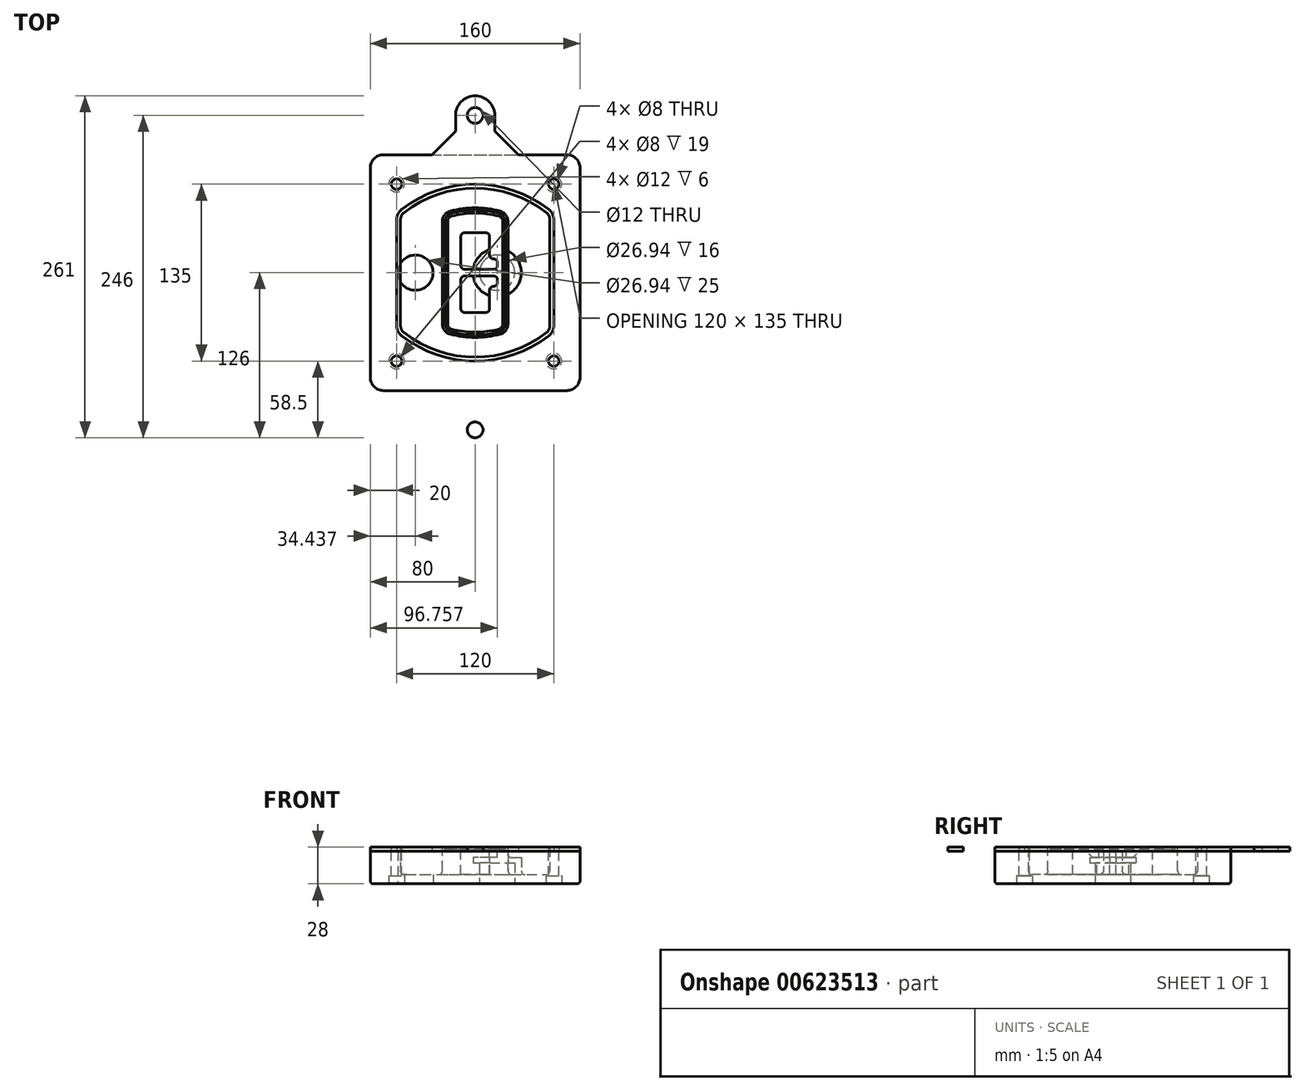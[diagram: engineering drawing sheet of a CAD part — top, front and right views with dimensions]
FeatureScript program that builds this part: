
annotation { "Feature Type Name" : "Feature", "Feature Type Description" : "" }
export const myFeature = defineFeature(function(context is Context, id is Id, definition is map)
    precondition{}
    {
        {
            var Q0;
            Q0=qCreatedBy(makeId("Top.planeOp"),FACE);
            var sketch = newSketch(context, id + "F0", { "sketchPlane" : qUnion([Q0])});
            skPoint(sketch, "E0.rect.middle", {"position": v(0, 0) * mm});
            skLineSegment(sketch, "E1.bottom", {"start": v(-70, -90) * mm, "end": v(70, -90) * mm});
            skLineSegment(sketch, "E1.top", {"start": v(-70, 90) * mm, "end": v(70, 90) * mm});
            skLineSegment(sketch, "E1.left", {"start": v(-80, -80) * mm, "end": v(-80, 80) * mm});
            skLineSegment(sketch, "E1.right", {"start": v(80, -80) * mm, "end": v(80, 80) * mm});
            skLineSegment(sketch, "E2", {"start": v(-80, 90) * mm, "end": v(80, -90) * mm, "construction": true});
            skLineSegment(sketch, "E3", {"start": v(80, 90) * mm, "end": v(-80, -90) * mm, "construction": true});
            skCircle(sketch, "E4", {"center": v(-60, 67.5) * mm, "radius": 4 * mm});
            skCircle(sketch, "E5", {"center": v(60, 67.5) * mm, "radius": 4 * mm});
            skCircle(sketch, "E6", {"center": v(60, -67.5) * mm, "radius": 4 * mm});
            skCircle(sketch, "E7", {"center": v(-60, -67.5) * mm, "radius": 4 * mm});
            skLineSegment(sketch, "E8", {"start": v(-60, 67.5) * mm, "end": v(60, 67.5) * mm, "construction": true});
            skLineSegment(sketch, "E9", {"start": v(60, 67.5) * mm, "end": v(60, -67.5) * mm, "construction": true});
            skLineSegment(sketch, "E10", {"start": v(60, -67.5) * mm, "end": v(-60, -67.5) * mm, "construction": true});
            skLineSegment(sketch, "E11", {"start": v(-60, -67.5) * mm, "end": v(-60, 67.5) * mm, "construction": true});
            skLineSegment(sketch, "E12", {"start": v(-60, 40.3) * mm, "end": v(-60, -40.3) * mm});
            skLineSegment(sketch, "E13", {"start": v(60, 40.3) * mm, "end": v(60, -40.3) * mm});
            skArc(sketch, "E14", {"start": v(56.15, 48.18) * mm, "mid": v(0, 67.5) * mm, "end": v(-56.15, 48.18) * mm});
            skArc(sketch, "E15", {"start": v(-56.15, -48.18) * mm, "mid": v(0, -67.5) * mm, "end": v(56.15, -48.18) * mm});
            skLineSegment(sketch, "E16", {"start": v(-60, 0) * mm, "end": v(60, 0) * mm, "construction": true});
            skPoint(sketch, "E17.visualSharp", {"position": v(-60, -45) * mm});
            skArc(sketch, "E17.filletArc", {"start": v(-60, -40.3) * mm, "mid": v(-58.99, -44.68) * mm, "end": v(-56.15, -48.18) * mm});
            skPoint(sketch, "E18.visualSharp", {"position": v(-60, 45) * mm});
            skArc(sketch, "E18.filletArc", {"start": v(-56.15, 48.18) * mm, "mid": v(-58.99, 44.68) * mm, "end": v(-60, 40.3) * mm});
            skPoint(sketch, "E19.visualSharp", {"position": v(60, 45) * mm});
            skArc(sketch, "E19.filletArc", {"start": v(60, 40.3) * mm, "mid": v(58.99, 44.68) * mm, "end": v(56.15, 48.18) * mm});
            skPoint(sketch, "E20.visualSharp", {"position": v(60, -45) * mm});
            skArc(sketch, "E20.filletArc", {"start": v(56.15, -48.18) * mm, "mid": v(58.99, -44.68) * mm, "end": v(60, -40.3) * mm});
            skPoint(sketch, "E21.visualSharp", {"position": v(-80, 90) * mm});
            skArc(sketch, "E21.filletArc", {"start": v(-70, 90) * mm, "mid": v(-77.07, 87.07) * mm, "end": v(-80, 80) * mm});
            skPoint(sketch, "E22.visualSharp", {"position": v(80, 90) * mm});
            skArc(sketch, "E22.filletArc", {"start": v(80, 80) * mm, "mid": v(77.07, 87.07) * mm, "end": v(70, 90) * mm});
            skPoint(sketch, "E23.visualSharp", {"position": v(80, -90) * mm});
            skArc(sketch, "E23.filletArc", {"start": v(70, -90) * mm, "mid": v(77.07, -87.07) * mm, "end": v(80, -80) * mm});
            skPoint(sketch, "E24.visualSharp", {"position": v(-80, -90) * mm});
            skArc(sketch, "E24.filletArc", {"start": v(-80, -80) * mm, "mid": v(-77.07, -87.07) * mm, "end": v(-70, -90) * mm});
            skArc(sketch, "E25.0", {"start": v(57, 40.3) * mm, "mid": v(56.3, 43.36) * mm, "end": v(54.3, 45.81) * mm});
            skLineSegment(sketch, "E25.1", {"start": v(57, 40.3) * mm, "end": v(57, -40.3) * mm});
            skArc(sketch, "E25.2", {"start": v(54.3, -45.81) * mm, "mid": v(56.3, -43.36) * mm, "end": v(57, -40.3) * mm});
            skArc(sketch, "E25.3", {"start": v(-54.3, -45.81) * mm, "mid": v(0, -64.5) * mm, "end": v(54.3, -45.81) * mm});
            skArc(sketch, "E25.4", {"start": v(-57, -40.3) * mm, "mid": v(-56.3, -43.36) * mm, "end": v(-54.3, -45.81) * mm});
            skArc(sketch, "E25.5", {"start": v(54.3, 45.81) * mm, "mid": v(0, 64.5) * mm, "end": v(-54.3, 45.81) * mm});
            skLineSegment(sketch, "E25.6", {"start": v(-57, 40.3) * mm, "end": v(-57, -40.3) * mm});
            skArc(sketch, "E25.7", {"start": v(-54.3, 45.81) * mm, "mid": v(-56.3, 43.36) * mm, "end": v(-57, 40.3) * mm});
            skArc(sketch, "E26.0", {"start": v(-58.62, 51.33) * mm, "mid": v(-62.58, 46.43) * mm, "end": v(-64, 40.3) * mm});
            skArc(sketch, "E26.1", {"start": v(58.62, 51.33) * mm, "mid": v(0, 71.5) * mm, "end": v(-58.62, 51.33) * mm});
            skArc(sketch, "E26.2", {"start": v(64, 40.3) * mm, "mid": v(62.58, 46.43) * mm, "end": v(58.62, 51.33) * mm});
            skLineSegment(sketch, "E26.3", {"start": v(64, 40.3) * mm, "end": v(64, -40.3) * mm});
            skArc(sketch, "E26.4", {"start": v(58.62, -51.33) * mm, "mid": v(62.58, -46.43) * mm, "end": v(64, -40.3) * mm});
            skLineSegment(sketch, "E26.5", {"start": v(-64, 40.3) * mm, "end": v(-64, -40.3) * mm});
            skArc(sketch, "E26.6", {"start": v(-58.62, -51.33) * mm, "mid": v(0, -71.5) * mm, "end": v(58.62, -51.33) * mm});
            skArc(sketch, "E26.7", {"start": v(-64, -40.3) * mm, "mid": v(-62.58, -46.43) * mm, "end": v(-58.62, -51.33) * mm});
            skSolve(sketch);
        }
        {
            var Q0;
            Q0=makeQuery(id+"F0.imprint","IMPRINT",FACE,{"disambiguationData":[TD([[makeQuery(id+"F0.imprint","IMPRINT",EDGE,{"derivedFrom":sQuery(id+"F0.wireOp",EDGE,"E1.bottom")}),1.0]])]});
            var Q1;
            Q1=makeQuery(id+"F0.imprint","IMPRINT",FACE,{"disambiguationData":[TD([[makeQuery(id+"F0.imprint","IMPRINT",EDGE,{"derivedFrom":sQuery(id+"F0.wireOp",EDGE,"E12")}),1.0]])]});
            var Q2;
            Q2=makeQuery(id+"F0.imprint","IMPRINT",FACE,{"disambiguationData":[TD([[makeQuery(id+"F0.imprint","IMPRINT",EDGE,{"derivedFrom":sQuery(id+"F0.wireOp",EDGE,"E25.0")}),1.0]])]});
            var Q3;
            Q3=makeQuery(id+"F0.imprint","IMPRINT",FACE,{"disambiguationData":[TD([[makeQuery(id+"F0.imprint","IMPRINT",EDGE,{"derivedFrom":sQuery(id+"F0.wireOp",EDGE,"E12")}),-1.0]])]});
            extrude(context, id + "F1", {"entities" : qUnion([Q0, Q1, Q2, Q3]), "oppositeDirection" : true, "depth" : 25 * mm});
        }
        {
            var Q0;
            Q0=makeQuery(id+"F0.imprint","IMPRINT",FACE,{"disambiguationData":[TD([[makeQuery(id+"F0.imprint","IMPRINT",EDGE,{"derivedFrom":sQuery(id+"F0.wireOp",EDGE,"E12")}),1.0]])]});
            extrude(context, id + "F2", {"entities" : qUnion([Q0]), "operationType" : NewBodyOperationType.ADD, "depth" : 3 * mm});
        }
        {
            var Q0;
            Q0=makeQuery(id+"F0.imprint","IMPRINT",FACE,{"disambiguationData":[TD([[makeQuery(id+"F0.imprint","IMPRINT",EDGE,{"derivedFrom":sQuery(id+"F0.wireOp",EDGE,"E25.0")}),1.0]])]});
            extrude(context, id + "F3", {"entities" : qUnion([Q0]), "operationType" : NewBodyOperationType.REMOVE, "oppositeDirection" : true, "depth" : 18 * mm});
        }
        {
            var Q0;
            Q0=makeQuery(id+"F2.opExtrude","CAP_FACE",FACE,{"disambiguationData":[OSD([sQuery(id+"F0.wireOp",EDGE,"E12"),sQuery(id+"F0.wireOp",EDGE,"E13"),sQuery(id+"F0.wireOp",EDGE,"E14"),sQuery(id+"F0.wireOp",EDGE,"E15"),sQuery(id+"F0.wireOp",EDGE,"E17.filletArc"),sQuery(id+"F0.wireOp",EDGE,"E18.filletArc"),sQuery(id+"F0.wireOp",EDGE,"E19.filletArc"),sQuery(id+"F0.wireOp",EDGE,"E20.filletArc"),sQuery(id+"F0.wireOp",EDGE,"E25.0"),sQuery(id+"F0.wireOp",EDGE,"E25.1"),sQuery(id+"F0.wireOp",EDGE,"E25.2"),sQuery(id+"F0.wireOp",EDGE,"E25.3"),sQuery(id+"F0.wireOp",EDGE,"E25.4"),sQuery(id+"F0.wireOp",EDGE,"E25.5"),sQuery(id+"F0.wireOp",EDGE,"E25.6"),sQuery(id+"F0.wireOp",EDGE,"E25.7")])],"isStart":false});
            var sketch = newSketch(context, id + "F4", { "sketchPlane" : qUnion([Q0])});
            skArc(sketch, "E27.0", {"start": v(-19.08, -46.97) * mm, "mid": v(0, -49.5) * mm, "end": v(19.08, -46.97) * mm});
            skArc(sketch, "E28.0", {"start": v(19.08, 46.97) * mm, "mid": v(0, 49.5) * mm, "end": v(-19.08, 46.97) * mm});
            skLineSegment(sketch, "E29", {"start": v(-25, 39.25) * mm, "end": v(-25, -39.25) * mm});
            skLineSegment(sketch, "E30", {"start": v(25, 39.25) * mm, "end": v(25, -39.25) * mm});
            skLineSegment(sketch, "E31", {"start": v(-25, 45.1) * mm, "end": v(25, 45.1) * mm, "construction": true});
            skLineSegment(sketch, "E32", {"start": v(-25, -45.1) * mm, "end": v(25, -45.1) * mm, "construction": true});
            skPoint(sketch, "E33.visualSharp", {"position": v(-25, 45.1) * mm});
            skArc(sketch, "E33.filletArc", {"start": v(-19.08, 46.97) * mm, "mid": v(-23.35, 44.11) * mm, "end": v(-25, 39.25) * mm});
            skPoint(sketch, "E34.visualSharp", {"position": v(25, 45.1) * mm});
            skArc(sketch, "E34.filletArc", {"start": v(25, 39.25) * mm, "mid": v(23.35, 44.11) * mm, "end": v(19.08, 46.97) * mm});
            skPoint(sketch, "E35.visualSharp", {"position": v(25, -45.1) * mm});
            skArc(sketch, "E35.filletArc", {"start": v(19.08, -46.97) * mm, "mid": v(23.35, -44.11) * mm, "end": v(25, -39.25) * mm});
            skPoint(sketch, "E36.visualSharp", {"position": v(-25, -45.1) * mm});
            skArc(sketch, "E36.filletArc", {"start": v(-25, -39.25) * mm, "mid": v(-23.35, -44.11) * mm, "end": v(-19.08, -46.97) * mm});
            skArc(sketch, "E37.0", {"start": v(54.3, 45.81) * mm, "mid": v(0, 64.5) * mm, "end": v(-54.3, 45.81) * mm});
            skArc(sketch, "E37.1", {"start": v(-54.3, 45.81) * mm, "mid": v(-56.3, 43.36) * mm, "end": v(-57, 40.3) * mm});
            skLineSegment(sketch, "E37.2", {"start": v(-57, 40.3) * mm, "end": v(-57, -40.3) * mm});
            skArc(sketch, "E37.3", {"start": v(-57, -40.3) * mm, "mid": v(-56.3, -43.36) * mm, "end": v(-54.3, -45.81) * mm});
            skArc(sketch, "E37.4", {"start": v(-54.3, -45.81) * mm, "mid": v(0, -64.5) * mm, "end": v(54.3, -45.81) * mm});
            skArc(sketch, "E37.5", {"start": v(54.3, -45.81) * mm, "mid": v(56.3, -43.36) * mm, "end": v(57, -40.3) * mm});
            skLineSegment(sketch, "E37.6", {"start": v(57, 40.3) * mm, "end": v(57, -40.3) * mm});
            skArc(sketch, "E37.7", {"start": v(57, 40.3) * mm, "mid": v(56.3, 43.36) * mm, "end": v(54.3, 45.81) * mm});
            skLineSegment(sketch, "E38.0", {"start": v(23, 39.25) * mm, "end": v(23, -39.25) * mm});
            skArc(sketch, "E38.1", {"start": v(18.56, -45.04) * mm, "mid": v(21.76, -42.9) * mm, "end": v(23, -39.25) * mm});
            skArc(sketch, "E38.2", {"start": v(-18.56, -45.04) * mm, "mid": v(0, -47.5) * mm, "end": v(18.56, -45.04) * mm});
            skArc(sketch, "E38.3", {"start": v(-23, -39.25) * mm, "mid": v(-21.76, -42.9) * mm, "end": v(-18.56, -45.04) * mm});
            skLineSegment(sketch, "E38.4", {"start": v(-23, 39.25) * mm, "end": v(-23, -39.25) * mm});
            skArc(sketch, "E38.5", {"start": v(23, 39.25) * mm, "mid": v(21.76, 42.9) * mm, "end": v(18.56, 45.04) * mm});
            skArc(sketch, "E38.6", {"start": v(-18.56, 45.04) * mm, "mid": v(-21.76, 42.9) * mm, "end": v(-23, 39.25) * mm});
            skArc(sketch, "E38.7", {"start": v(18.56, 45.04) * mm, "mid": v(0, 47.5) * mm, "end": v(-18.56, 45.04) * mm});
            skArc(sketch, "E39.0", {"start": v(21, 39.25) * mm, "mid": v(20.18, 41.68) * mm, "end": v(18.04, 43.1) * mm});
            skLineSegment(sketch, "E39.1", {"start": v(21, 39.25) * mm, "end": v(21, -39.25) * mm});
            skArc(sketch, "E39.2", {"start": v(18.04, -43.1) * mm, "mid": v(20.18, -41.68) * mm, "end": v(21, -39.25) * mm});
            skArc(sketch, "E39.3", {"start": v(-18.04, -43.1) * mm, "mid": v(0, -45.5) * mm, "end": v(18.04, -43.1) * mm});
            skArc(sketch, "E39.4", {"start": v(-21, -39.25) * mm, "mid": v(-20.18, -41.68) * mm, "end": v(-18.04, -43.1) * mm});
            skArc(sketch, "E39.5", {"start": v(18.04, 43.1) * mm, "mid": v(0, 45.5) * mm, "end": v(-18.04, 43.1) * mm});
            skLineSegment(sketch, "E39.6", {"start": v(-21, 39.25) * mm, "end": v(-21, -39.25) * mm});
            skArc(sketch, "E39.7", {"start": v(-18.04, 43.1) * mm, "mid": v(-20.18, 41.68) * mm, "end": v(-21, 39.25) * mm});
            skLineSegment(sketch, "E40", {"start": v(-25, 0) * mm, "end": v(25, 0) * mm, "construction": true});
            skLineSegment(sketch, "E41", {"start": v(-11, 5.5) * mm, "end": v(-11, 27.5) * mm});
            skLineSegment(sketch, "E42", {"start": v(-8, 30.5) * mm, "end": v(8, 30.5) * mm});
            skLineSegment(sketch, "E43", {"start": v(11, 27.5) * mm, "end": v(11, 13.5) * mm});
            skLineSegment(sketch, "E44", {"start": v(14, 10.5) * mm, "end": v(14, 10.5) * mm});
            skLineSegment(sketch, "E45", {"start": v(17, 7.5) * mm, "end": v(17, 5.5) * mm});
            skLineSegment(sketch, "E46", {"start": v(14, 2.5) * mm, "end": v(-8, 2.5) * mm});
            skPoint(sketch, "E47.visualSharp", {"position": v(-11, 30.5) * mm});
            skArc(sketch, "E47.filletArc", {"start": v(-8, 30.5) * mm, "mid": v(-10.12, 29.62) * mm, "end": v(-11, 27.5) * mm});
            skPoint(sketch, "E48.visualSharp", {"position": v(11, 30.5) * mm});
            skArc(sketch, "E48.filletArc", {"start": v(11, 27.5) * mm, "mid": v(10.12, 29.62) * mm, "end": v(8, 30.5) * mm});
            skPoint(sketch, "E49.visualSharp", {"position": v(11, 10.5) * mm});
            skArc(sketch, "E49.filletArc", {"start": v(11, 13.5) * mm, "mid": v(11.88, 11.38) * mm, "end": v(14, 10.5) * mm});
            skPoint(sketch, "E50.visualSharp", {"position": v(17, 10.5) * mm});
            skArc(sketch, "E50.filletArc", {"start": v(17, 7.5) * mm, "mid": v(16.12, 9.62) * mm, "end": v(14, 10.5) * mm});
            skPoint(sketch, "E51.visualSharp", {"position": v(17, 2.5) * mm});
            skArc(sketch, "E51.filletArc", {"start": v(14, 2.5) * mm, "mid": v(16.12, 3.38) * mm, "end": v(17, 5.5) * mm});
            skPoint(sketch, "E52.visualSharp", {"position": v(-11, 2.5) * mm});
            skArc(sketch, "E52.filletArc", {"start": v(-11, 5.5) * mm, "mid": v(-10.12, 3.38) * mm, "end": v(-8, 2.5) * mm});
            skLineSegment(sketch, "E53.0.MirrorCS", {"start": v(14, -2.5) * mm, "end": v(-8, -2.5) * mm});
            skArc(sketch, "E54.0.MirrorCS", {"start": v(-11, -5.5) * mm, "mid": v(-10.12, -3.38) * mm, "end": v(-8, -2.5) * mm});
            skLineSegment(sketch, "E55.0.MirrorCS", {"start": v(-11, -5.5) * mm, "end": v(-11, -27.5) * mm});
            skArc(sketch, "E56.0.MirrorCS", {"start": v(-8, -30.5) * mm, "mid": v(-10.12, -29.62) * mm, "end": v(-11, -27.5) * mm});
            skLineSegment(sketch, "E57.0.MirrorCS", {"start": v(-8, -30.5) * mm, "end": v(8, -30.5) * mm});
            skArc(sketch, "E58.0.MirrorCS", {"start": v(11, -27.5) * mm, "mid": v(10.12, -29.62) * mm, "end": v(8, -30.5) * mm});
            skLineSegment(sketch, "E59.0.MirrorCS", {"start": v(11, -27.5) * mm, "end": v(11, -13.5) * mm});
            skArc(sketch, "E60.0.MirrorCS", {"start": v(11, -13.5) * mm, "mid": v(11.88, -11.38) * mm, "end": v(14, -10.5) * mm});
            skArc(sketch, "E61.0.MirrorCS", {"start": v(17, -7.5) * mm, "mid": v(16.12, -9.62) * mm, "end": v(14, -10.5) * mm});
            skLineSegment(sketch, "E62.0.MirrorCS", {"start": v(17, -7.5) * mm, "end": v(17, -5.5) * mm});
            skArc(sketch, "E63.0.MirrorCS", {"start": v(14, -2.5) * mm, "mid": v(16.12, -3.38) * mm, "end": v(17, -5.5) * mm});
            skSolve(sketch);
        }
        {
            var Q0;
            Q0=makeQuery(id+"F4.imprint","IMPRINT",FACE,{"disambiguationData":[TD([[makeQuery(id+"F4.imprint","IMPRINT",EDGE,{"derivedFrom":sQuery(id+"F4.wireOp",EDGE,"E27.0")}),1.0]])]});
            var Q1;
            Q1=makeQuery(id+"F4.imprint","IMPRINT",FACE,{"disambiguationData":[TD([[makeQuery(id+"F4.imprint","IMPRINT",EDGE,{"derivedFrom":sQuery(id+"F4.wireOp",EDGE,"E38.0")}),-1.0]])]});
            var Q2;
            Q2=makeQuery(id+"F4.imprint","IMPRINT",FACE,{"disambiguationData":[TD([[makeQuery(id+"F4.imprint","IMPRINT",EDGE,{"derivedFrom":sQuery(id+"F4.wireOp",EDGE,"E39.0")}),1.0]])]});
            extrude(context, id + "F5", {"entities" : qUnion([Q0, Q1, Q2]), "operationType" : NewBodyOperationType.ADD, "endBound" : BoundingType.UP_TO_NEXT, "oppositeDirection" : true, "depth" : 25 * mm});
        }
        {
            var Q0;
            Q0=makeQuery(id+"F4.imprint","IMPRINT",FACE,{"disambiguationData":[TD([[makeQuery(id+"F4.imprint","IMPRINT",EDGE,{"derivedFrom":sQuery(id+"F4.wireOp",EDGE,"E38.0")}),-1.0]])]});
            extrude(context, id + "F6", {"entities" : qUnion([Q0]), "operationType" : NewBodyOperationType.REMOVE, "oppositeDirection" : true, "depth" : 2 * mm});
        }
        {
            var Q0;
            Q0=makeQuery(id+"F1.opExtrude","CAP_FACE",FACE,{"disambiguationData":[OSD([sQuery(id+"F0.wireOp",EDGE,"E1.bottom"),sQuery(id+"F0.wireOp",EDGE,"E1.top"),sQuery(id+"F0.wireOp",EDGE,"E1.left"),sQuery(id+"F0.wireOp",EDGE,"E1.right"),sQuery(id+"F0.wireOp",EDGE,"E4"),sQuery(id+"F0.wireOp",EDGE,"E5"),sQuery(id+"F0.wireOp",EDGE,"E6"),sQuery(id+"F0.wireOp",EDGE,"E7"),sQuery(id+"F0.wireOp",EDGE,"E21.filletArc"),sQuery(id+"F0.wireOp",EDGE,"E22.filletArc"),sQuery(id+"F0.wireOp",EDGE,"E23.filletArc"),sQuery(id+"F0.wireOp",EDGE,"E24.filletArc")])],"isStart":false});
            var sketch = newSketch(context, id + "F7", { "sketchPlane" : qUnion([Q0])});
            skCircle(sketch, "E64", {"center": v(16.76, 0) * mm, "radius": 13.47 * mm});
            skCircle(sketch, "E65", {"center": v(-45.56, 0) * mm, "radius": 13.47 * mm});
            skLineSegment(sketch, "E66", {"start": v(80, 0) * mm, "end": v(-80, 0) * mm});
            skCircle(sketch, "E67", {"center": v(16.76, 0) * mm, "radius": 18.47 * mm});
            skCircle(sketch, "E68", {"center": v(60, -67.5) * mm, "radius": 6 * mm});
            skCircle(sketch, "E69", {"center": v(-60, -67.5) * mm, "radius": 6 * mm});
            skCircle(sketch, "E70", {"center": v(-60, 67.5) * mm, "radius": 6 * mm});
            skCircle(sketch, "E71", {"center": v(60, 67.5) * mm, "radius": 6 * mm});
            skSolve(sketch);
        }
        {
            var Q0;
            {var subQ1=sQuery(id+"F7.wireOp",EDGE,"E66");var subQ4=sQuery(id+"F7.wireOp",EDGE,"E64");var subQ6=makeQuery(id+"F7.imprint","INTERSECT",VERTEX,{"disambiguationData":[OD(0.0)],"derivedFrom":[subQ4,subQ1]});Q0=makeQuery(id+"F7.imprint","IMPRINT",FACE,{"disambiguationData":[TD([[makeQuery(id+"F7.imprint","IMPRINT",EDGE,{"disambiguationData":[TD([[subQ6,-1.0]])],"derivedFrom":subQ4}),-1.0]])]});}
            var Q1;
            {var subQ0=sQuery(id+"F7.wireOp",EDGE,"E66");var subQ1=sQuery(id+"F7.wireOp",EDGE,"E64");var subQ3=makeQuery(id+"F7.imprint","INTERSECT",VERTEX,{"disambiguationData":[OD(0.0)],"derivedFrom":[subQ1,subQ0]});Q1=makeQuery(id+"F7.imprint","IMPRINT",FACE,{"disambiguationData":[TD([[makeQuery(id+"F7.imprint","IMPRINT",EDGE,{"disambiguationData":[TD([[subQ3,-1.0]])],"derivedFrom":subQ1}),1.0]])]});}
            var Q2;
            {var subQ0=sQuery(id+"F7.wireOp",EDGE,"E66");var subQ1=sQuery(id+"F7.wireOp",EDGE,"E64");var subQ3=makeQuery(id+"F7.imprint","INTERSECT",VERTEX,{"disambiguationData":[OD(0.0)],"derivedFrom":[subQ1,subQ0]});Q2=makeQuery(id+"F7.imprint","IMPRINT",FACE,{"disambiguationData":[TD([[makeQuery(id+"F7.imprint","IMPRINT",EDGE,{"disambiguationData":[TD([[subQ3,1.0]])],"derivedFrom":subQ1}),1.0]])]});}
            var Q3;
            {var subQ1=sQuery(id+"F7.wireOp",EDGE,"E66");var subQ4=sQuery(id+"F7.wireOp",EDGE,"E64");var subQ6=makeQuery(id+"F7.imprint","INTERSECT",VERTEX,{"disambiguationData":[OD(0.0)],"derivedFrom":[subQ4,subQ1]});Q3=makeQuery(id+"F7.imprint","IMPRINT",FACE,{"disambiguationData":[TD([[makeQuery(id+"F7.imprint","IMPRINT",EDGE,{"disambiguationData":[TD([[subQ6,1.0]])],"derivedFrom":subQ4}),-1.0]])]});}
            extrude(context, id + "F8", {"entities" : qUnion([Q0, Q1, Q2, Q3]), "operationType" : NewBodyOperationType.ADD, "oppositeDirection" : true, "depth" : 20 * mm});
        }
        {
            var Q0;
            {var subQ0=sQuery(id+"F7.wireOp",EDGE,"E66");var subQ1=sQuery(id+"F7.wireOp",EDGE,"E64");var subQ3=makeQuery(id+"F7.imprint","INTERSECT",VERTEX,{"disambiguationData":[OD(0.0)],"derivedFrom":[subQ1,subQ0]});Q0=makeQuery(id+"F7.imprint","IMPRINT",FACE,{"disambiguationData":[TD([[makeQuery(id+"F7.imprint","IMPRINT",EDGE,{"disambiguationData":[TD([[subQ3,-1.0]])],"derivedFrom":subQ1}),1.0]])]});}
            var Q1;
            {var subQ0=sQuery(id+"F7.wireOp",EDGE,"E66");var subQ1=sQuery(id+"F7.wireOp",EDGE,"E64");var subQ3=makeQuery(id+"F7.imprint","INTERSECT",VERTEX,{"disambiguationData":[OD(0.0)],"derivedFrom":[subQ1,subQ0]});Q1=makeQuery(id+"F7.imprint","IMPRINT",FACE,{"disambiguationData":[TD([[makeQuery(id+"F7.imprint","IMPRINT",EDGE,{"disambiguationData":[TD([[subQ3,1.0]])],"derivedFrom":subQ1}),1.0]])]});}
            extrude(context, id + "F9", {"entities" : qUnion([Q0, Q1]), "operationType" : NewBodyOperationType.REMOVE, "oppositeDirection" : true, "depth" : 16 * mm});
        }
        {
            var Q0;
            {var subQ0=sQuery(id+"F7.wireOp",EDGE,"E66");var subQ1=sQuery(id+"F7.wireOp",EDGE,"E65");var subQ3=makeQuery(id+"F7.imprint","INTERSECT",VERTEX,{"disambiguationData":[OD(0.0)],"derivedFrom":[subQ1,subQ0]});Q0=makeQuery(id+"F7.imprint","IMPRINT",FACE,{"disambiguationData":[TD([[makeQuery(id+"F7.imprint","IMPRINT",EDGE,{"disambiguationData":[TD([[subQ3,-1.0]])],"derivedFrom":subQ1}),1.0]])]});}
            var Q1;
            {var subQ0=sQuery(id+"F7.wireOp",EDGE,"E66");var subQ1=sQuery(id+"F7.wireOp",EDGE,"E65");var subQ3=makeQuery(id+"F7.imprint","INTERSECT",VERTEX,{"disambiguationData":[OD(0.0)],"derivedFrom":[subQ1,subQ0]});Q1=makeQuery(id+"F7.imprint","IMPRINT",FACE,{"disambiguationData":[TD([[makeQuery(id+"F7.imprint","IMPRINT",EDGE,{"disambiguationData":[TD([[subQ3,1.0]])],"derivedFrom":subQ1}),1.0]])]});}
            extrude(context, id + "F10", {"entities" : qUnion([Q0, Q1]), "operationType" : NewBodyOperationType.REMOVE, "oppositeDirection" : true, "depth" : 25 * mm});
        }
        {
            var Q0;
            Q0=makeQuery(id+"F7.imprint","IMPRINT",FACE,{"disambiguationData":[TD([[makeQuery(id+"F7.imprint","IMPRINT",EDGE,{"derivedFrom":sQuery(id+"F7.wireOp",EDGE,"E68")}),1.0]])]});
            var Q1;
            Q1=makeQuery(id+"F7.imprint","IMPRINT",FACE,{"disambiguationData":[TD([[makeQuery(id+"F7.imprint","IMPRINT",EDGE,{"derivedFrom":makeQuery(id+"F1.opExtrude","CAP_EDGE",EDGE,{"disambiguationData":[OSD([sQuery(id+"F0.wireOp",EDGE,"E5")])],"isStart":false})}),-1.0]])]});
            var Q2;
            Q2=makeQuery(id+"F7.imprint","IMPRINT",FACE,{"disambiguationData":[TD([[makeQuery(id+"F7.imprint","IMPRINT",EDGE,{"derivedFrom":sQuery(id+"F7.wireOp",EDGE,"E69")}),1.0]])]});
            var Q3;
            Q3=makeQuery(id+"F7.imprint","IMPRINT",FACE,{"disambiguationData":[TD([[makeQuery(id+"F7.imprint","IMPRINT",EDGE,{"derivedFrom":makeQuery(id+"F1.opExtrude","CAP_EDGE",EDGE,{"disambiguationData":[OSD([sQuery(id+"F0.wireOp",EDGE,"E4")])],"isStart":false})}),-1.0]])]});
            var Q4;
            Q4=makeQuery(id+"F7.imprint","IMPRINT",FACE,{"disambiguationData":[TD([[makeQuery(id+"F7.imprint","IMPRINT",EDGE,{"derivedFrom":sQuery(id+"F7.wireOp",EDGE,"E70")}),1.0]])]});
            var Q5;
            Q5=makeQuery(id+"F7.imprint","IMPRINT",FACE,{"disambiguationData":[TD([[makeQuery(id+"F7.imprint","IMPRINT",EDGE,{"derivedFrom":makeQuery(id+"F1.opExtrude","CAP_EDGE",EDGE,{"disambiguationData":[OSD([sQuery(id+"F0.wireOp",EDGE,"E7")])],"isStart":false})}),-1.0]])]});
            var Q6;
            Q6=makeQuery(id+"F7.imprint","IMPRINT",FACE,{"disambiguationData":[TD([[makeQuery(id+"F7.imprint","IMPRINT",EDGE,{"derivedFrom":sQuery(id+"F7.wireOp",EDGE,"E71")}),1.0]])]});
            var Q7;
            Q7=makeQuery(id+"F7.imprint","IMPRINT",FACE,{"disambiguationData":[TD([[makeQuery(id+"F7.imprint","IMPRINT",EDGE,{"derivedFrom":makeQuery(id+"F1.opExtrude","CAP_EDGE",EDGE,{"disambiguationData":[OSD([sQuery(id+"F0.wireOp",EDGE,"E6")])],"isStart":false})}),-1.0]])]});
            extrude(context, id + "F11", {"entities" : qUnion([Q0, Q1, Q2, Q3, Q4, Q5, Q6, Q7]), "operationType" : NewBodyOperationType.REMOVE, "oppositeDirection" : true, "depth" : 6 * mm});
        }
        {
            var Q0;
            Q0=makeQuery(id+"F9.boolean.opBoolean","COPY",FACE,{"derivedFrom":makeQuery(id+"F9.opExtrude","CAP_FACE",FACE,{"disambiguationData":[OSD([sQuery(id+"F7.wireOp",EDGE,"E64")])],"isStart":false})});
            var sketch = newSketch(context, id + "F12", { "sketchPlane" : qUnion([Q0])});
            skArc(sketch, "E72.0", {"start": v(11, 17.55) * mm, "mid": v(2.57, 11.82) * mm, "end": v(-1.54, 2.5) * mm});
            skArc(sketch, "E72.1", {"start": v(-1.54, -2.5) * mm, "mid": v(2.57, -11.82) * mm, "end": v(11, -17.55) * mm});
            skLineSegment(sketch, "E73", {"start": v(-1.54, -2.5) * mm, "end": v(14, -2.5) * mm});
            skLineSegment(sketch, "E74.0", {"start": v(14, 2.5) * mm, "end": v(-1.54, 2.5) * mm});
            skArc(sketch, "E74.1", {"start": v(14, 2.5) * mm, "mid": v(16.12, 3.38) * mm, "end": v(17, 5.5) * mm});
            skLineSegment(sketch, "E74.2", {"start": v(17, 7.5) * mm, "end": v(17, 5.5) * mm});
            skArc(sketch, "E74.3", {"start": v(17, 7.5) * mm, "mid": v(16.12, 9.62) * mm, "end": v(14, 10.5) * mm});
            skArc(sketch, "E74.4", {"start": v(11, 13.5) * mm, "mid": v(11.88, 11.38) * mm, "end": v(14, 10.5) * mm});
            skLineSegment(sketch, "E74.5", {"start": v(11, 17.55) * mm, "end": v(11, 13.5) * mm});
            skLineSegment(sketch, "E74.7", {"start": v(14, -2.5) * mm, "end": v(-1.54, -2.5) * mm});
            skArc(sketch, "E74.8", {"start": v(14, -2.5) * mm, "mid": v(16.12, -3.38) * mm, "end": v(17, -5.5) * mm});
            skLineSegment(sketch, "E74.9", {"start": v(17, -7.5) * mm, "end": v(17, -5.5) * mm});
            skArc(sketch, "E74.10", {"start": v(17, -7.5) * mm, "mid": v(16.12, -9.62) * mm, "end": v(14, -10.5) * mm});
            skArc(sketch, "E74.11", {"start": v(11, -13.5) * mm, "mid": v(11.88, -11.38) * mm, "end": v(14, -10.5) * mm});
            skLineSegment(sketch, "E74.12", {"start": v(11, -17.55) * mm, "end": v(11, -13.5) * mm});
            skPoint(sketch, "E75.orphan", {"position": v(11, -27.5) * mm});
            skPoint(sketch, "E76.orphan", {"position": v(-8, -2.5) * mm});
            skPoint(sketch, "E77.orphan", {"position": v(-8, 2.5) * mm});
            skPoint(sketch, "E78.orphan", {"position": v(11, 27.5) * mm});
            skSolve(sketch);
        }
        {
            var Q0;
            {var subQ7=sQuery(id+"F12.wireOp",EDGE,"E72.0");var subQ14=sQuery(id+"F12.wireOp",EDGE,"E72.1");var subQ16=sQuery(id+"F12.wireOp",EDGE,"E74.1");var subQ18=sQuery(id+"F12.wireOp",EDGE,"E74.8");Q0=qUnion([makeQuery(id+"F12.imprint","IMPRINT",FACE,{"disambiguationData":[TD([[makeQuery(id+"F12.imprint","IMPRINT",EDGE,{"derivedFrom":subQ7}),1.0]])]}),makeQuery(id+"F12.imprint","IMPRINT",FACE,{"disambiguationData":[TD([[makeQuery(id+"F12.imprint","IMPRINT",EDGE,{"derivedFrom":subQ14}),1.0]])]}),makeQuery(id+"F12.imprint","IMPRINT",FACE,{"disambiguationData":[TD([[makeQuery(id+"F12.imprint","IMPRINT",EDGE,{"derivedFrom":subQ16}),1.0]])]}),makeQuery(id+"F12.imprint","IMPRINT",FACE,{"disambiguationData":[TD([[makeQuery(id+"F12.imprint","IMPRINT",EDGE,{"derivedFrom":subQ18}),-1.0]])]})]);}
            var Q1;
            Q1=makeQuery(id+"F5.boolean.opBoolean","SPLIT",FACE,{"disambiguationData":[TD([makeQuery(id+"F5.opExtrude","SWEPT_FACE",FACE,{"disambiguationData":[OSD([sQuery(id+"F4.wireOp",EDGE,"E41")])]})])],"derivedFrom":makeQuery(id+"F3.boolean.opBoolean","COPY",FACE,{"derivedFrom":makeQuery(id+"F3.opExtrude","CAP_FACE",FACE,{"disambiguationData":[OSD([sQuery(id+"F0.wireOp",EDGE,"E25.0"),sQuery(id+"F0.wireOp",EDGE,"E25.1"),sQuery(id+"F0.wireOp",EDGE,"E25.2"),sQuery(id+"F0.wireOp",EDGE,"E25.3"),sQuery(id+"F0.wireOp",EDGE,"E25.4"),sQuery(id+"F0.wireOp",EDGE,"E25.5"),sQuery(id+"F0.wireOp",EDGE,"E25.6"),sQuery(id+"F0.wireOp",EDGE,"E25.7")])],"isStart":false})})});
            extrude(context, id + "F13", {"entities" : qUnion([Q0]), "operationType" : NewBodyOperationType.REMOVE, "endBound" : BoundingType.UP_TO_SURFACE, "endBoundEntityFace" : qUnion([Q1]), "depth" : 25 * mm});
        }
        {
            var Q0;
            Q0=makeQuery(id+"F3.boolean.opBoolean","COPY",EDGE,{"derivedFrom":makeQuery(id+"F3.opExtrude","CAP_EDGE",EDGE,{"disambiguationData":[OSD([sQuery(id+"F0.wireOp",EDGE,"E25.6")])],"isStart":false})});
            var Q1;
            Q1=makeQuery(id+"F8.boolean.opBoolean","INTERSECT",EDGE,{"derivedFrom":[makeQuery(id+"F5.opExtrude","SWEPT_FACE",FACE,{"disambiguationData":[OSD([sQuery(id+"F4.wireOp",EDGE,"E30")])]}),makeQuery(id+"F8.opExtrude","CAP_FACE",FACE,{"disambiguationData":[OSD([sQuery(id+"F7.wireOp",EDGE,"E67")])],"isStart":false})]});
            var Q2;
            Q2=makeQuery(id+"F8.boolean.opBoolean","INTERSECT",EDGE,{"disambiguationData":[OD(1.0)],"derivedFrom":[makeQuery(id+"F5.opExtrude","SWEPT_FACE",FACE,{"disambiguationData":[OSD([sQuery(id+"F4.wireOp",EDGE,"E30")])]}),makeQuery(id+"F8.opExtrude","SWEPT_FACE",FACE,{"disambiguationData":[OSD([sQuery(id+"F7.wireOp",EDGE,"E67")])]})]});
            var Q3;
            {var subQ0=sQuery(id+"F4.wireOp",EDGE,"E30");Q3=makeQuery(id+"F8.boolean.opBoolean","SPLIT",EDGE,{"disambiguationData":[TD([makeQuery(id+"F5.opExtrude","SWEPT_FACE",FACE,{"disambiguationData":[OSD([sQuery(id+"F4.wireOp",EDGE,"E35.filletArc")])]})])],"derivedFrom":makeQuery(id+"F5.opExtrude","CAP_EDGE",EDGE,{"disambiguationData":[OSD([subQ0])],"isStart":false})});}
            var Q4;
            {var subQ0=sQuery(id+"F0.wireOp",EDGE,"E25.7");var subQ1=sQuery(id+"F0.wireOp",EDGE,"E25.1");var subQ2=sQuery(id+"F0.wireOp",EDGE,"E25.6");var subQ3=sQuery(id+"F0.wireOp",EDGE,"E25.5");var subQ4=sQuery(id+"F0.wireOp",EDGE,"E25.4");var subQ5=sQuery(id+"F0.wireOp",EDGE,"E25.0");var subQ6=sQuery(id+"F0.wireOp",EDGE,"E25.2");var subQ7=sQuery(id+"F0.wireOp",EDGE,"E25.3");Q4=makeQuery(id+"F8.boolean.opBoolean","INTERSECT",EDGE,{"derivedFrom":[makeQuery(id+"F5.boolean.opBoolean","SPLIT",FACE,{"disambiguationData":[TD([makeQuery(id+"F2.opExtrude","SWEPT_FACE",FACE,{"disambiguationData":[OSD([subQ5])]})])],"derivedFrom":makeQuery(id+"F3.boolean.opBoolean","COPY",FACE,{"derivedFrom":makeQuery(id+"F3.opExtrude","CAP_FACE",FACE,{"disambiguationData":[OSD([subQ5,subQ1,subQ6,subQ7,subQ4,subQ3,subQ2,subQ0])],"isStart":false})})}),makeQuery(id+"F8.opExtrude","SWEPT_FACE",FACE,{"disambiguationData":[OSD([sQuery(id+"F7.wireOp",EDGE,"E67")])]})]});}
            var Q5;
            Q5=makeQuery(id+"F8.boolean.opBoolean","INTERSECT",EDGE,{"disambiguationData":[OD(0.0)],"derivedFrom":[makeQuery(id+"F5.opExtrude","SWEPT_FACE",FACE,{"disambiguationData":[OSD([sQuery(id+"F4.wireOp",EDGE,"E30")])]}),makeQuery(id+"F8.opExtrude","SWEPT_FACE",FACE,{"disambiguationData":[OSD([sQuery(id+"F7.wireOp",EDGE,"E67")])]})]});
            fillet(context, id + "F14", {"entities" : qUnion([Q0, Q1, Q2, Q3, Q4, Q5]), "radius" : 3 * mm, "tangentPropagation" : true, "allowEdgeOverflow" : false});
        }
        {
            var Q0;
            Q0=makeQuery(id+"F1.opExtrude","CAP_EDGE",EDGE,{"disambiguationData":[OSD([sQuery(id+"F0.wireOp",EDGE,"E1.bottom")])],"isStart":false});
            fillet(context, id + "F15", {"entities" : qUnion([Q0]), "radius" : 2 * mm, "tangentPropagation" : true, "allowEdgeOverflow" : false});
        }
        {
            var Q0;
            {var subQ0=sQuery(id+"F0.wireOp",EDGE,"E21.filletArc");var subQ1=sQuery(id+"F0.wireOp",EDGE,"E7");var subQ2=sQuery(id+"F0.wireOp",EDGE,"E6");var subQ3=sQuery(id+"F0.wireOp",EDGE,"E5");var subQ4=sQuery(id+"F0.wireOp",EDGE,"E4");var subQ5=sQuery(id+"F0.wireOp",EDGE,"E22.filletArc");var subQ6=sQuery(id+"F0.wireOp",EDGE,"E1.bottom");var subQ7=sQuery(id+"F0.wireOp",EDGE,"E1.right");var subQ8=sQuery(id+"F0.wireOp",EDGE,"E1.top");var subQ9=sQuery(id+"F0.wireOp",EDGE,"E1.left");var subQ10=sQuery(id+"F0.wireOp",EDGE,"E23.filletArc");var subQ11=sQuery(id+"F0.wireOp",EDGE,"E24.filletArc");Q0=makeQuery(id+"F2.boolean.opBoolean","SPLIT",FACE,{"disambiguationData":[TD([makeQuery(id+"F1.opExtrude","SWEPT_FACE",FACE,{"disambiguationData":[OSD([subQ6])]})])],"derivedFrom":makeQuery(id+"F1.opExtrude","CAP_FACE",FACE,{"disambiguationData":[OSD([subQ6,subQ8,subQ9,subQ7,subQ4,subQ3,subQ2,subQ1,subQ0,subQ5,subQ10,subQ11])],"isStart":true})});}
            var sketch = newSketch(context, id + "F16", { "sketchPlane" : qUnion([Q0])});
            skArc(sketch, "E79.0", {"start": v(-70, 90) * mm, "mid": v(-77.07, 87.07) * mm, "end": v(-80, 80) * mm});
            skLineSegment(sketch, "E79.1", {"start": v(-70, 90) * mm, "end": v(70, 90) * mm});
            skLineSegment(sketch, "E79.2", {"start": v(-80, -80) * mm, "end": v(-80, 80) * mm});
            skCircle(sketch, "E79.3", {"center": v(-60, 67.5) * mm, "radius": 4 * mm});
            skArc(sketch, "E79.4", {"start": v(56.15, 48.18) * mm, "mid": v(0, 67.5) * mm, "end": v(-56.15, 48.18) * mm});
            skArc(sketch, "E79.5", {"start": v(-56.15, 48.18) * mm, "mid": v(-58.99, 44.68) * mm, "end": v(-60, 40.3) * mm});
            skLineSegment(sketch, "E79.6", {"start": v(-60, 40.3) * mm, "end": v(-60, -40.3) * mm});
            skLineSegment(sketch, "E80", {"start": v(0, 90) * mm, "end": v(0, 120) * mm, "construction": true});
            skPoint(sketch, "E80.endSnap0", {"position": v(0, 90) * mm});
            skCircle(sketch, "E81", {"center": v(0, 120) * mm, "radius": 6 * mm});
            skArc(sketch, "E82", {"start": v(15, 120) * mm, "mid": v(0, 135) * mm, "end": v(-15, 120) * mm});
            skLineSegment(sketch, "E83.MirrorCS", {"start": v(-15, 108) * mm, "end": v(-33, 90) * mm});
            skLineSegment(sketch, "E84", {"start": v(-15, 120) * mm, "end": v(-15, 108) * mm});
            skLineSegment(sketch, "E85.MirrorCS", {"start": v(15, 120) * mm, "end": v(15, 108) * mm});
            skLineSegment(sketch, "E86.MirrorCS", {"start": v(15, 108) * mm, "end": v(33, 90) * mm});
            skLineSegment(sketch, "E87.0", {"start": v(-70, -90) * mm, "end": v(70, -90) * mm});
            skArc(sketch, "E87.1", {"start": v(-80, -80) * mm, "mid": v(-77.07, -87.07) * mm, "end": v(-70, -90) * mm});
            skArc(sketch, "E87.2", {"start": v(70, -90) * mm, "mid": v(77.07, -87.07) * mm, "end": v(80, -80) * mm});
            skLineSegment(sketch, "E87.3", {"start": v(80, -80) * mm, "end": v(80, 80) * mm});
            skArc(sketch, "E87.4", {"start": v(80, 80) * mm, "mid": v(77.07, 87.07) * mm, "end": v(70, 90) * mm});
            skLineSegment(sketch, "E88", {"start": v(-60, 0) * mm, "end": v(60, 0) * mm, "construction": true});
            skLineSegment(sketch, "E89.MirrorCS", {"start": v(-15, -120) * mm, "end": v(-15, -108) * mm});
            skLineSegment(sketch, "E90.MirrorCS", {"start": v(-15, -108) * mm, "end": v(-33, -90) * mm});
            skCircle(sketch, "E91.MirrorC", {"center": v(0, -120) * mm, "radius": 6 * mm});
            skArc(sketch, "E92.MirrorCS", {"start": v(15, -120) * mm, "mid": v(0, -135) * mm, "end": v(-15, -120) * mm});
            skLineSegment(sketch, "E93.MirrorCS", {"start": v(0, -90) * mm, "end": v(0, -120) * mm, "construction": true});
            skLineSegment(sketch, "E94.MirrorCS", {"start": v(15, -120) * mm, "end": v(15, -108) * mm});
            skPoint(sketch, "E95.MirrorP", {"position": v(0, -90) * mm});
            skLineSegment(sketch, "E96.MirrorCS", {"start": v(15, -108) * mm, "end": v(33, -90) * mm});
            skSolve(sketch);
        }
        {
            var Q0;
            Q0=makeQuery(id+"F16.imprint","IMPRINT",FACE,{"disambiguationData":[TD([[makeQuery(id+"F16.imprint","IMPRINT",EDGE,{"derivedFrom":sQuery(id+"F16.wireOp",EDGE,"E81")}),-1.0]])]});
            var Q1;
            Q1=makeQuery(id+"F16.imprint","IMPRINT",FACE,{"disambiguationData":[TD([[makeQuery(id+"F16.imprint","IMPRINT",EDGE,{"derivedFrom":sQuery(id+"F16.wireOp",EDGE,"E91.MirrorC")}),1.0]])]});
            var Q2;
            {var subQ9=sQuery(id+"F16.wireOp",EDGE,"E79.0");Q2=makeQuery(id+"F16.imprint","IMPRINT",FACE,{"disambiguationData":[TD([[makeQuery(id+"F16.imprint","IMPRINT",EDGE,{"derivedFrom":subQ9}),1.0]])]});}
            var Q3;
            Q3=makeQuery(id+"F2.opExtrude","CAP_FACE",FACE,{"disambiguationData":[OSD([sQuery(id+"F0.wireOp",EDGE,"E12"),sQuery(id+"F0.wireOp",EDGE,"E13"),sQuery(id+"F0.wireOp",EDGE,"E14"),sQuery(id+"F0.wireOp",EDGE,"E15"),sQuery(id+"F0.wireOp",EDGE,"E17.filletArc"),sQuery(id+"F0.wireOp",EDGE,"E18.filletArc"),sQuery(id+"F0.wireOp",EDGE,"E19.filletArc"),sQuery(id+"F0.wireOp",EDGE,"E20.filletArc"),sQuery(id+"F0.wireOp",EDGE,"E25.0"),sQuery(id+"F0.wireOp",EDGE,"E25.1"),sQuery(id+"F0.wireOp",EDGE,"E25.2"),sQuery(id+"F0.wireOp",EDGE,"E25.3"),sQuery(id+"F0.wireOp",EDGE,"E25.4"),sQuery(id+"F0.wireOp",EDGE,"E25.5"),sQuery(id+"F0.wireOp",EDGE,"E25.6"),sQuery(id+"F0.wireOp",EDGE,"E25.7")])],"isStart":false});
            extrude(context, id + "F17", {"entities" : qUnion([Q0, Q1, Q2]), "endBound" : BoundingType.UP_TO_SURFACE, "depth" : 25 * mm, "endBoundEntityFace" : qUnion([Q3]), "offsetDistance" : 25 * mm});
        }
    });
